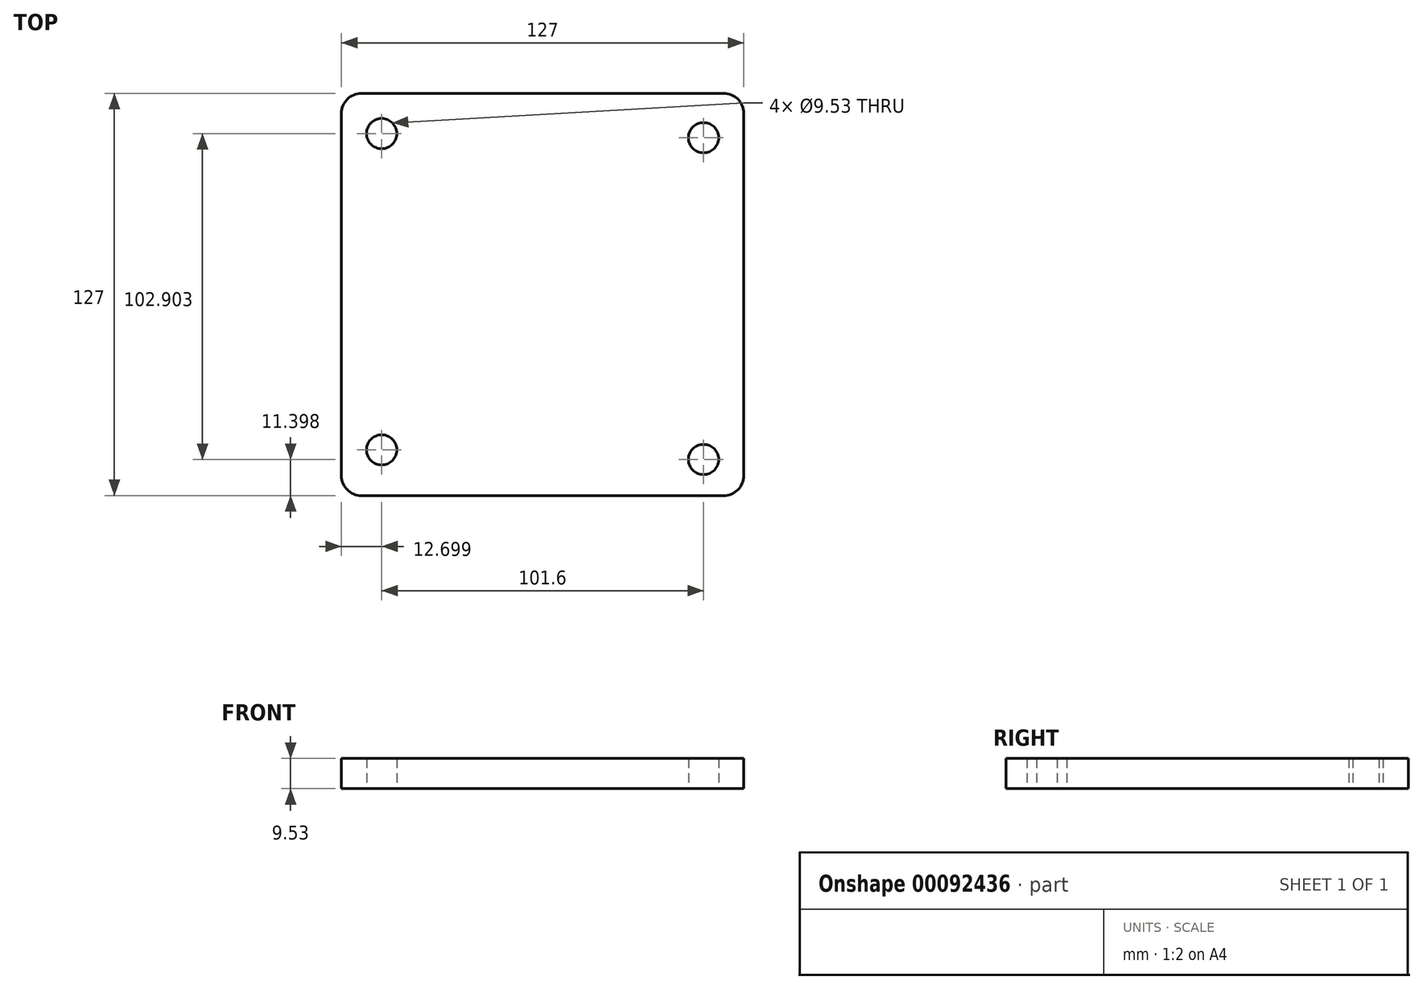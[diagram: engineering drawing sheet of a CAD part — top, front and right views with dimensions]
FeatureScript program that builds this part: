
annotation { "Feature Type Name" : "Feature", "Feature Type Description" : "" }
export const myFeature = defineFeature(function(context is Context, id is Id, definition is map)
    precondition{}
    {
        {
            var Q0;
            Q0=qCreatedBy(makeId("Top.planeOp"),FACE);
            var sketch = newSketch(context, id + "F0", { "sketchPlane" : qUnion([Q0])});
            skLineSegment(sketch, "E0.bottom", {"start": v(-72.01, 60.97) * mm, "end": v(54.99, 60.97) * mm});
            skLineSegment(sketch, "E0.top", {"start": v(-72.01, -66.03) * mm, "end": v(54.99, -66.03) * mm});
            skLineSegment(sketch, "E0.left", {"start": v(-72.01, 60.97) * mm, "end": v(-72.01, -66.03) * mm});
            skLineSegment(sketch, "E0.right", {"start": v(54.99, 60.97) * mm, "end": v(54.99, -66.03) * mm});
            skCircle(sketch, "E1", {"center": v(-59.31, 48.27) * mm, "radius": 4.76 * mm});
            skCircle(sketch, "E2", {"center": v(42.29, 46.97) * mm, "radius": 4.76 * mm});
            skCircle(sketch, "E3", {"center": v(42.29, -54.63) * mm, "radius": 4.76 * mm});
            skCircle(sketch, "E4", {"center": v(-59.31, -51.59) * mm, "radius": 4.76 * mm});
            skSolve(sketch);
        }
        {
            var Q0;
            Q0=makeQuery(id+"F0.imprint","IMPRINT",FACE,{"disambiguationData":[TD([[makeQuery(id+"F0.imprint","IMPRINT",EDGE,{"derivedFrom":sQuery(id+"F0.wireOp",EDGE,"E0.bottom")}),-1.0]])]});
            extrude(context, id + "F1", {"entities" : qUnion([Q0]), "depth" : 9.52 * mm});
        }
        {
            var Q0;
            Q0=makeQuery(id+"F1.opExtrude","SWEPT_EDGE",EDGE,{"disambiguationData":[OSD([sQuery(id+"F0.wireOp",EDGE,"E0.top"),sQuery(id+"F0.wireOp",EDGE,"E0.left")])]});
            var Q1;
            Q1=makeQuery(id+"F1.opExtrude","SWEPT_EDGE",EDGE,{"disambiguationData":[OSD([sQuery(id+"F0.wireOp",EDGE,"E0.top"),sQuery(id+"F0.wireOp",EDGE,"E0.right")])]});
            var Q2;
            Q2=makeQuery(id+"F1.opExtrude","SWEPT_EDGE",EDGE,{"disambiguationData":[OSD([sQuery(id+"F0.wireOp",EDGE,"E0.bottom"),sQuery(id+"F0.wireOp",EDGE,"E0.left")])]});
            var Q3;
            Q3=makeQuery(id+"F1.opExtrude","SWEPT_EDGE",EDGE,{"disambiguationData":[OSD([sQuery(id+"F0.wireOp",EDGE,"E0.bottom"),sQuery(id+"F0.wireOp",EDGE,"E0.right")])]});
            fillet(context, id + "F2", {"entities" : qUnion([Q0, Q1, Q2, Q3]), "radius" : 6.35 * mm, "tangentPropagation" : true, "allowEdgeOverflow" : false});
        }
    });
